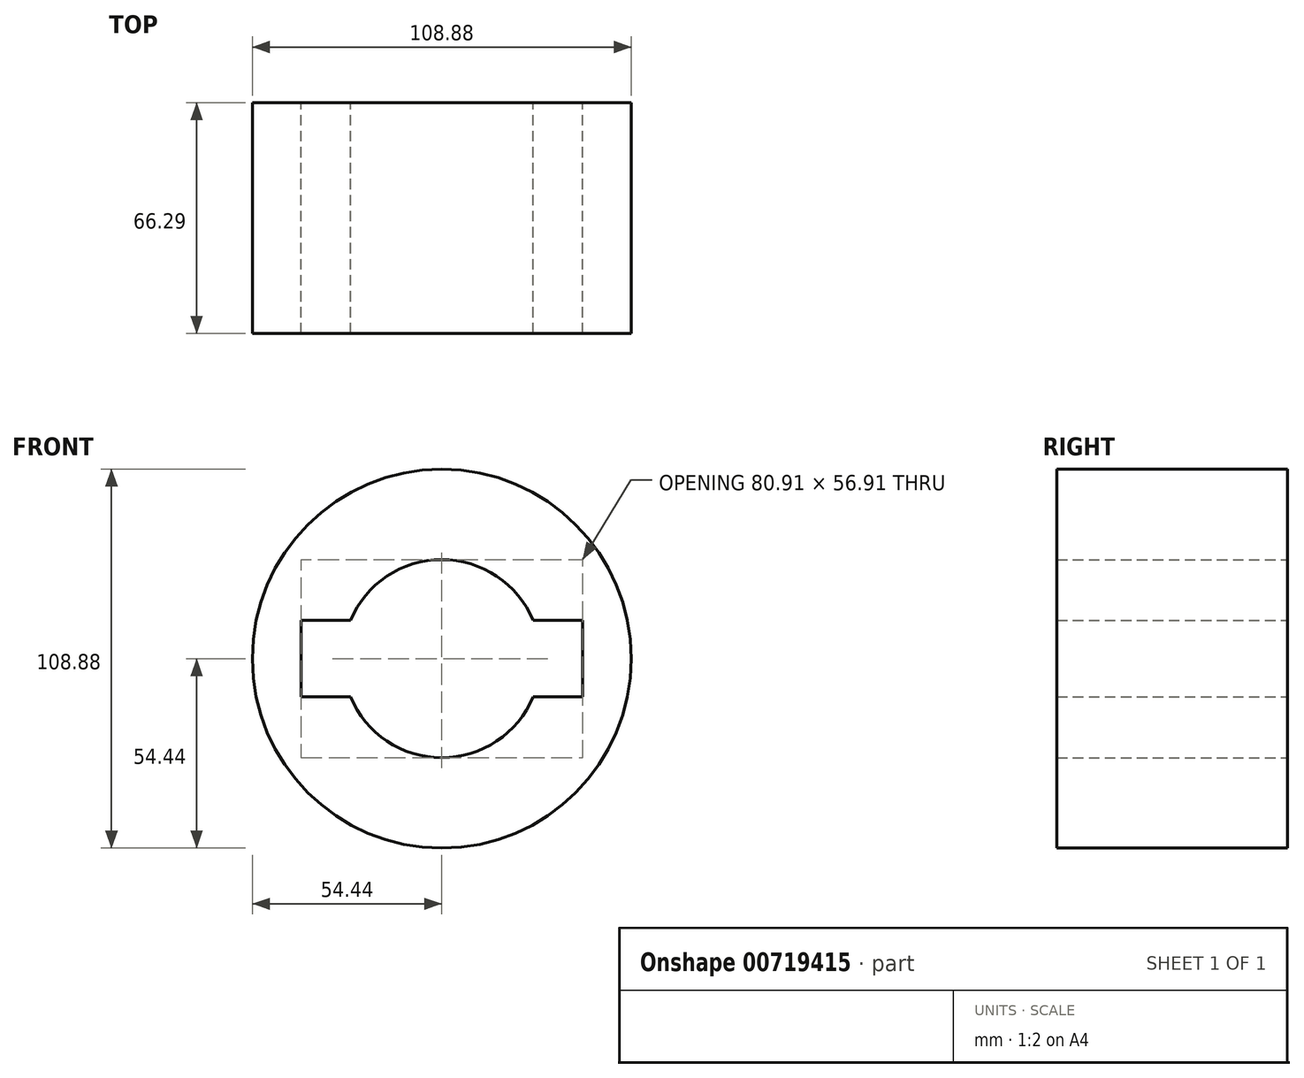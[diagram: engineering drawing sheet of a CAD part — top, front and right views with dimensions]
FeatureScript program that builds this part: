
annotation { "Feature Type Name" : "Feature", "Feature Type Description" : "" }
export const myFeature = defineFeature(function(context is Context, id is Id, definition is map)
    precondition{}
    {
        {
            var Q0;
            Q0=qCreatedBy(makeId("Front.planeOp"),FACE);
            var sketch = newSketch(context, id + "F0", { "sketchPlane" : qUnion([Q0])});
            skCircle(sketch, "E0", {"center": v(0, 0) * mm, "radius": 54.44 * mm});
            skCircle(sketch, "E1", {"center": v(0, 0) * mm, "radius": 28.46 * mm});
            skPoint(sketch, "E2.middle", {"position": v(3.68, 0) * mm});
            skLineSegment(sketch, "E3.bottom", {"start": v(-40.46, 10.98) * mm, "end": v(40.46, 10.98) * mm});
            skLineSegment(sketch, "E3.top", {"start": v(-40.46, -10.98) * mm, "end": v(40.46, -10.98) * mm});
            skLineSegment(sketch, "E3.left", {"start": v(-40.46, 10.98) * mm, "end": v(-40.46, -10.98) * mm});
            skLineSegment(sketch, "E3.right", {"start": v(40.46, 10.98) * mm, "end": v(40.46, -10.98) * mm});
            skSolve(sketch);
        }
        {
            var Q0;
            Q0 = qSketchRegion(id + "F0", true);
            extrude(context, id + "F1", {"entities" : qUnion([Q0]), "depth" : 66.3 * mm, "offsetDistance" : 25.4 * mm});
        }
    });
